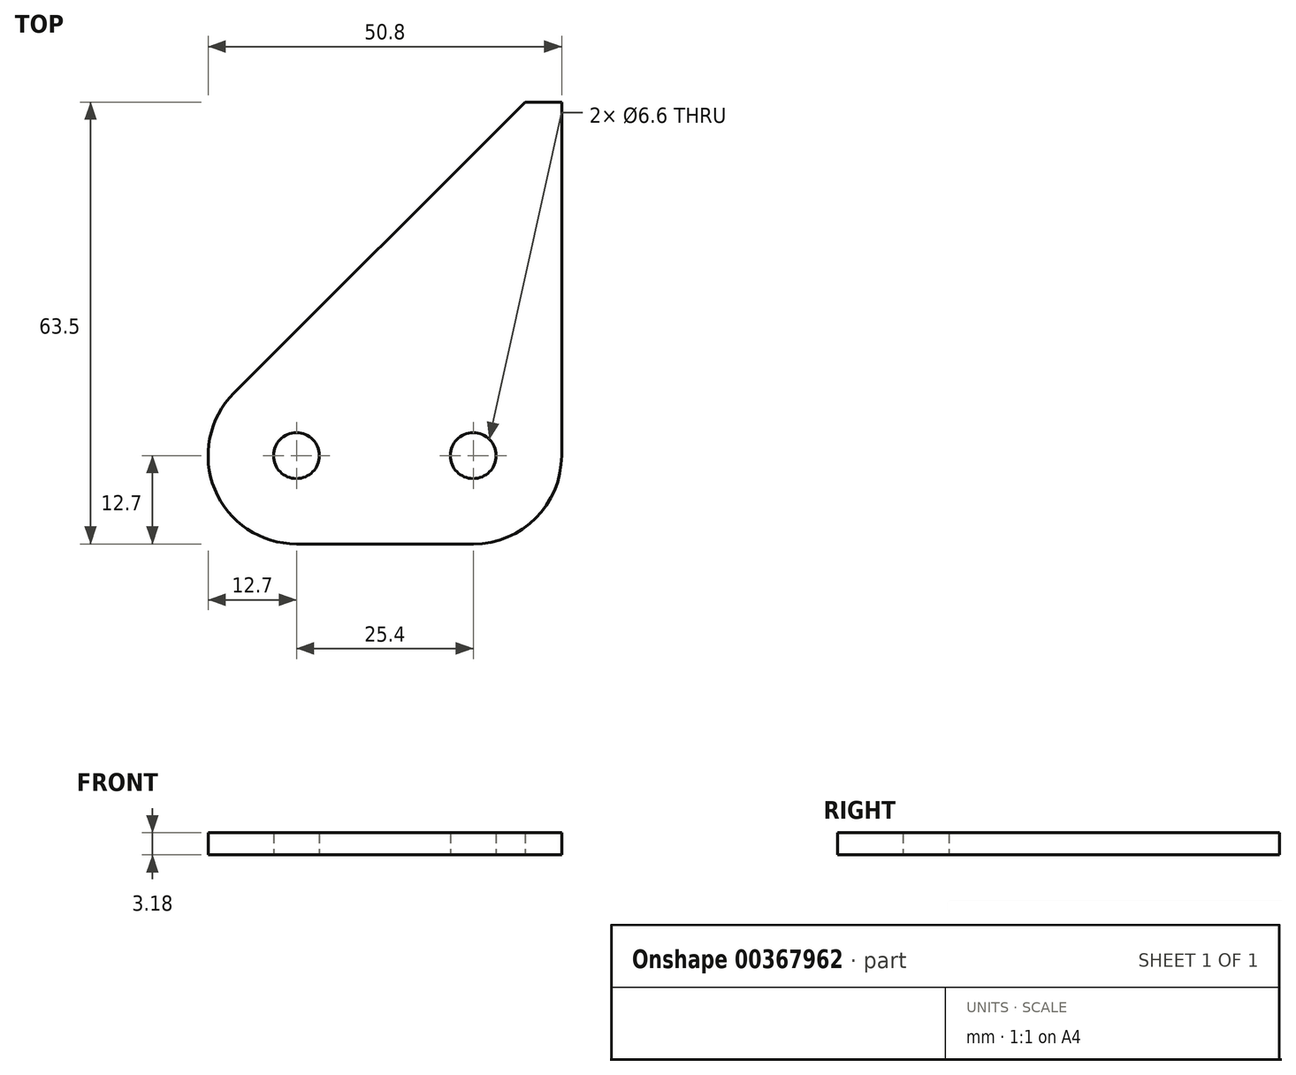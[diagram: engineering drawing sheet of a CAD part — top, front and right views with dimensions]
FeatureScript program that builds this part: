
annotation { "Feature Type Name" : "Feature", "Feature Type Description" : "" }
export const myFeature = defineFeature(function(context is Context, id is Id, definition is map)
    precondition{}
    {
        {
            var Q0;
            Q0=qCreatedBy(makeId("Top.planeOp"),FACE);
            var sketch = newSketch(context, id + "F0", { "sketchPlane" : qUnion([Q0])});
            skLineSegment(sketch, "E0", {"start": v(-47.08, 21.68) * mm, "end": v(-5.26, 63.5) * mm});
            skLineSegment(sketch, "E1", {"start": v(0, 63.5) * mm, "end": v(0, 12.7) * mm});
            skLineSegment(sketch, "E2", {"start": v(-12.7, 0) * mm, "end": v(-38.1, 0) * mm});
            skPoint(sketch, "E3.visualSharp", {"position": v(-68.76, 0) * mm});
            skArc(sketch, "E3.filletArc", {"start": v(-47.08, 21.68) * mm, "mid": v(-49.83, 7.84) * mm, "end": v(-38.1, 0) * mm});
            skPoint(sketch, "E4.visualSharp", {"position": v(0, 0) * mm});
            skArc(sketch, "E4.filletArc", {"start": v(-12.7, 0) * mm, "mid": v(-3.72, 3.72) * mm, "end": v(0, 12.7) * mm});
            skCircle(sketch, "E5", {"center": v(-38.1, 12.7) * mm, "radius": 3.3 * mm});
            skCircle(sketch, "E6", {"center": v(-12.7, 12.7) * mm, "radius": 3.3 * mm});
            skLineSegment(sketch, "E7", {"start": v(-5.26, 63.5) * mm, "end": v(0, 63.5) * mm});
            skSolve(sketch);
        }
        {
            var Q0;
            Q0=makeQuery(id+"F0.imprint","IMPRINT",FACE,{"disambiguationData":[TD([[makeQuery(id+"F0.imprint","IMPRINT",EDGE,{"derivedFrom":sQuery(id+"F0.wireOp",EDGE,"E0")}),-1.0]])]});
            extrude(context, id + "F1", {"entities" : qUnion([Q0]), "depth" : 3.17 * mm});
        }
    });
